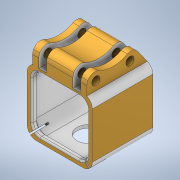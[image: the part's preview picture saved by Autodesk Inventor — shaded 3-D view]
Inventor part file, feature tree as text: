
AUTODESK INVENTOR PART (.ipt)
format: ipt  version: 2020 (Build 240168000, 168)  size: 334,848 bytes
history: native  units: in
note: dims shown in document units (in); Inventor stores cm internally (conversion verified against a paired STEP export)
features: extrude x5, sketch x5, other x3, projected_geometry x3, fillet x2
ambient origin geometry x8: Origin, YZ Plane, XZ Plane, XY Plane, X Axis, Y Axis, Z Axis, Center Point
bodies: Solid1 (feature_tree)
feature tree (18):
  other  "Assembly4.iam"
  other  "Kauri modular session 5 mount.ipt:1"
  other  "session 5.ipt:1"
  extrude  "Extrusion1"  Depth=0.3937in TaperAngle=0.0deg
  extrude  "Extrusion2"  Depth=1.0in TaperAngle=0.0deg
  extrude  "Extrusion3"  Depth=0.3937in TaperAngle=0.0deg
  fillet  "Fillet1"  Radius=0.2362in
  fillet  "Fillet2"  Radius=0.0394in
  extrude  "Extrusion4"  Depth=0.3937in
  extrude  "Extrusion5"  Depth=0.1969in
  sketch  "Sketch1"  dims[d0=0.3937in d1=1.0in d2=0.0in]
  projected_geometry  "Projected Loop1"
  sketch  "Sketch2"  dims[d3=0.5906in d4=1.0in d5=0.0in]
  sketch  "Sketch3"  dims[d6=0.9843in d7=0.3937in d8=0.0in d9=0.2362in d10=0.0394in]
  projected_geometry  "Projected Loop2"
  sketch  "Sketch4"  dims[d12=0.0197in d15=0.3937in d16=0.0in d17=0.0197in]
  projected_geometry  "Projected Loop3"
  sketch  "Sketch5"  dims[d18=0.0197in d19=0.0197in d20=0.0197in d21=0.1575in d22=0.1575in d23=0.1575in d24=0.0in d25=0.0in d26=0.1969in d27=0.1969in]
